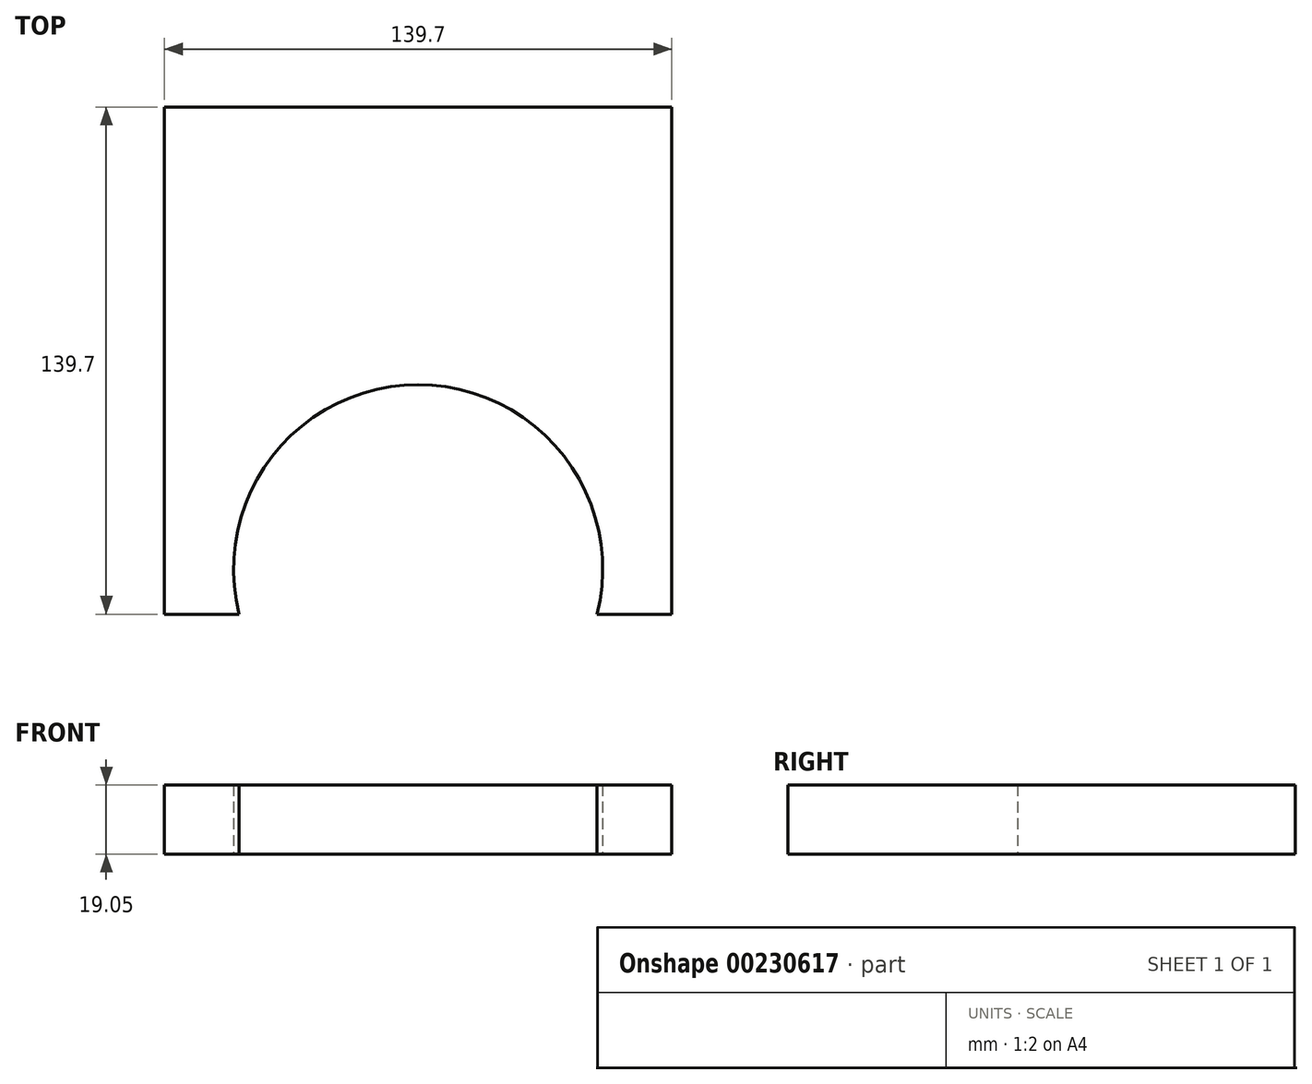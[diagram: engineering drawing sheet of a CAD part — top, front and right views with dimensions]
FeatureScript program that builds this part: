
annotation { "Feature Type Name" : "Feature", "Feature Type Description" : "" }
export const myFeature = defineFeature(function(context is Context, id is Id, definition is map)
    precondition{}
    {
        {
            var Q0;
            Q0=qCreatedBy(makeId("Top.planeOp"),FACE);
            var sketch = newSketch(context, id + "F0", { "sketchPlane" : qUnion([Q0])});
            skLineSegment(sketch, "E0.bottom", {"start": v(-69.85, 69.85) * mm, "end": v(69.85, 69.85) * mm});
            skLineSegment(sketch, "E0.top", {"start": v(-69.85, -69.85) * mm, "end": v(-49.25, -69.85) * mm});
            skLineSegment(sketch, "E0.left", {"start": v(-69.85, 69.85) * mm, "end": v(-69.85, -69.85) * mm});
            skLineSegment(sketch, "E0.right", {"start": v(69.85, 69.85) * mm, "end": v(69.85, -69.85) * mm});
            skPoint(sketch, "E0.middle", {"position": v(0, 0) * mm});
            skArc(sketch, "E1", {"start": v(49.25, -69.85) * mm, "mid": v(0, -6.6) * mm, "end": v(-49.25, -69.85) * mm});
            skLineSegment(sketch, "E2.trimOffspring", {"start": v(49.25, -69.85) * mm, "end": v(69.85, -69.85) * mm});
            skSolve(sketch);
        }
        {
            var Q0;
            Q0=makeQuery(id+"F0.imprint","IMPRINT",FACE,{"disambiguationData":[TD([[makeQuery(id+"F0.imprint","IMPRINT",EDGE,{"derivedFrom":sQuery(id+"F0.wireOp",EDGE,"E0.bottom")}),-1.0]])]});
            extrude(context, id + "F1", {"entities" : qUnion([Q0]), "depth" : 19.05 * mm});
        }
    });
